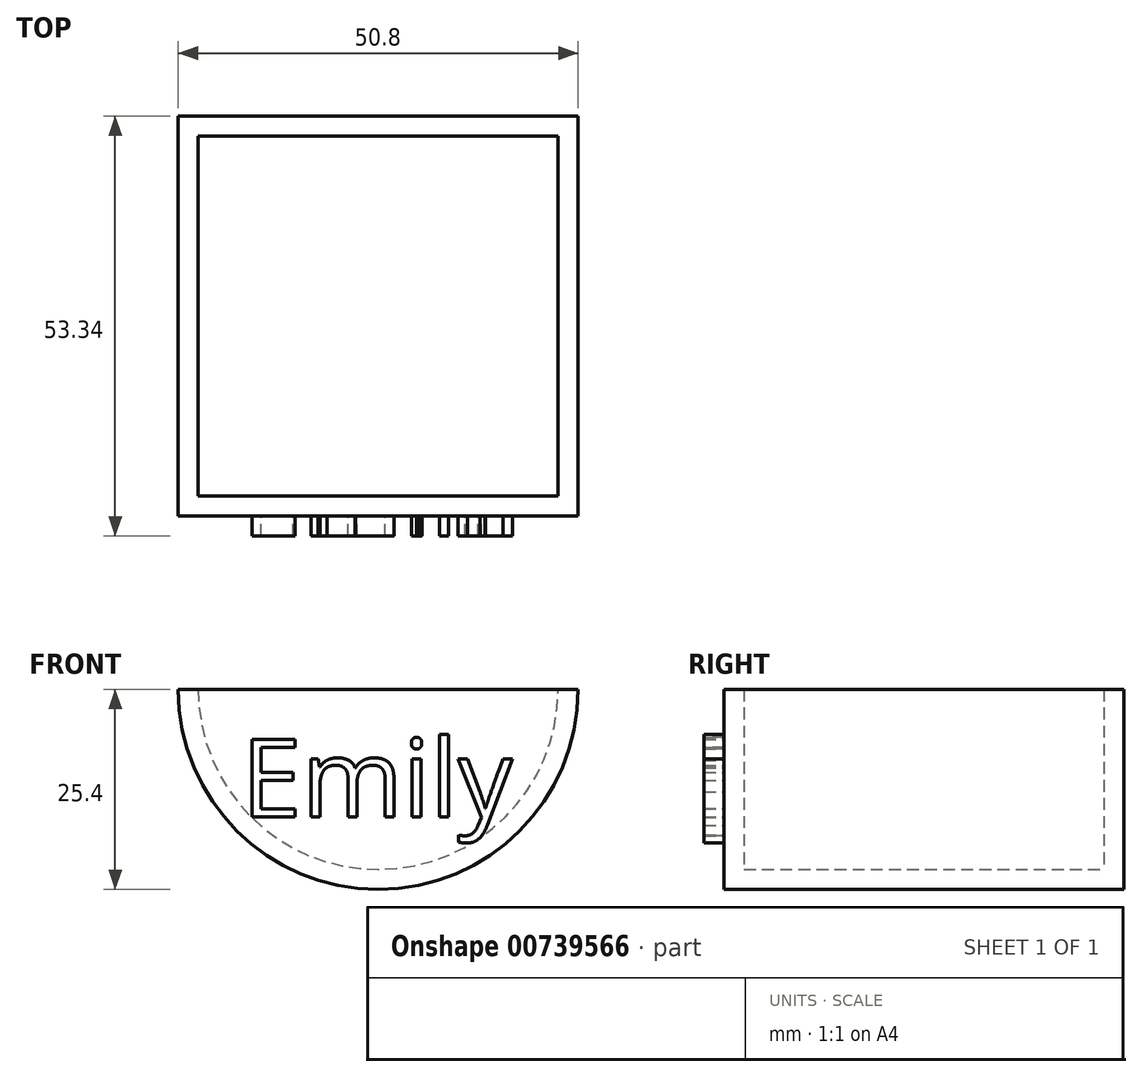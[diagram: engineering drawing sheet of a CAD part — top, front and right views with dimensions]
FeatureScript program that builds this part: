
annotation { "Feature Type Name" : "Feature", "Feature Type Description" : "" }
export const myFeature = defineFeature(function(context is Context, id is Id, definition is map)
    precondition{}
    {
        {
            var Q0;
            Q0=qCreatedBy(makeId("Front.planeOp"),FACE);
            var sketch = newSketch(context, id + "F0", { "sketchPlane" : qUnion([Q0])});
            skLineSegment(sketch, "E0", {"start": v(0, 0) * mm, "end": v(25.4, 0) * mm});
            skLineSegment(sketch, "E1", {"start": v(0, 0) * mm, "end": v(-25.4, 0) * mm});
            skLineSegment(sketch, "E2", {"start": v(0, 0) * mm, "end": v(0, -25.4) * mm});
            skPoint(sketch, "E3.start.orphan", {"position": v(0, -27.6) * mm});
            skArc(sketch, "E4", {"start": v(-25.4, 0) * mm, "mid": v(0, -25.4) * mm, "end": v(25.4, 0) * mm});
            skSolve(sketch);
        }
        {
            var Q0;
            {var subQ0=sQuery(id+"F0.wireOp",EDGE,"E0");Q0=makeQuery(id+"F0.imprint","IMPRINT",FACE,{"disambiguationData":[TD([[makeQuery(id+"F0.imprint","IMPRINT",EDGE,{"derivedFrom":subQ0}),-1.0]])]});}
            var Q1;
            {var subQ0=sQuery(id+"F0.wireOp",EDGE,"E1");Q1=makeQuery(id+"F0.imprint","IMPRINT",FACE,{"disambiguationData":[TD([[makeQuery(id+"F0.imprint","IMPRINT",EDGE,{"derivedFrom":subQ0}),1.0]])]});}
            extrude(context, id + "F1", {"entities" : qUnion([Q0, Q1]), "depth" : 50.8 * mm, "offsetDistance" : 25.4 * mm});
        }
        {
            var Q0;
            Q0=makeQuery(id+"F1.opExtrude","SWEPT_FACE",FACE,{"disambiguationData":[OSD([sQuery(id+"F0.wireOp",EDGE,"E0"),sQuery(id+"F0.wireOp",EDGE,"E1")])]});
            shell(context, id + "F2", {"entities" : qUnion([Q0]), "thickness" : 2.54 * mm});
        }
        {
            var Q0;
            Q0=makeQuery(id+"F1.opExtrude","CAP_FACE",FACE,{"disambiguationData":[OSD([sQuery(id+"F0.wireOp",EDGE,"E0"),sQuery(id+"F0.wireOp",EDGE,"E1"),sQuery(id+"F0.wireOp",EDGE,"E4")])],"isStart":false});
            var sketch = newSketch(context, id + "F3", { "sketchPlane" : qUnion([Q0])});
            skText(sketch, "E5", { "text": "Emily", "fontName": "OpenSans-Regular.ttf"});
            const initialGuessF3  = {"E5": [-0.01737, -0.0162, 1, 0, 0.00993]};
            skSetInitialGuess(sketch, initialGuessF3);
            skSolve(sketch);
        }
        {
            var Q0;
            Q0 = qSketchRegion(id + "F3", true);
            extrude(context, id + "F4", {"entities" : qUnion([Q0]), "operationType" : NewBodyOperationType.ADD, "depth" : 2.54 * mm, "offsetDistance" : 25.4 * mm});
        }
    });
